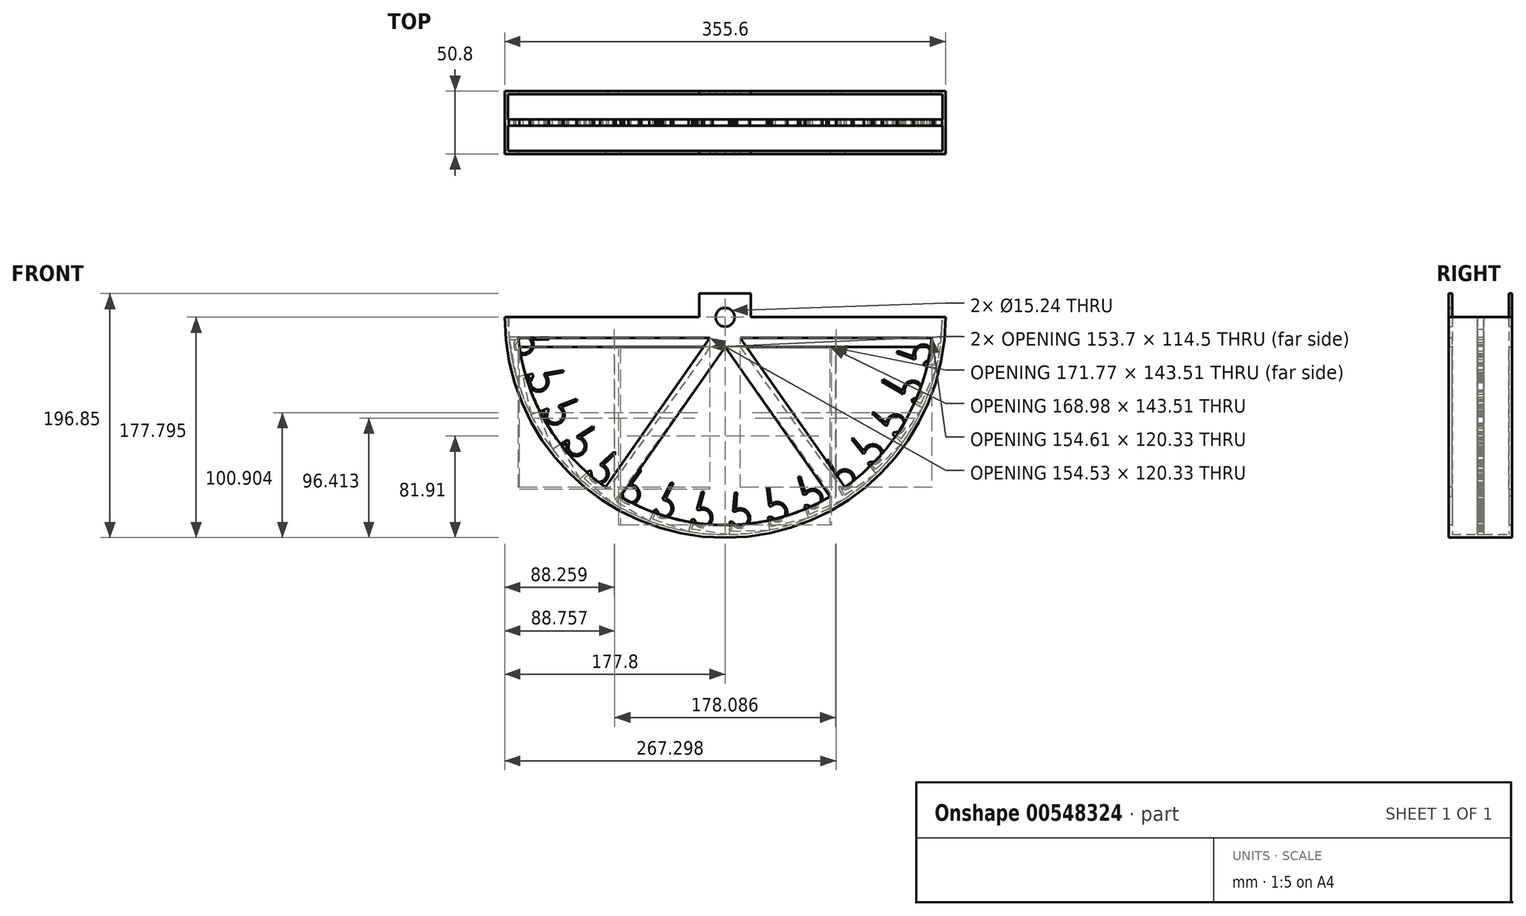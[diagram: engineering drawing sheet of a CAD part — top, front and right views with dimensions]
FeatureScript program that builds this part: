
annotation { "Feature Type Name" : "Feature", "Feature Type Description" : "" }
export const myFeature = defineFeature(function(context is Context, id is Id, definition is map)
    precondition{}
    {
        {
            var Q0;
            Q0=qCreatedBy(makeId("Front.planeOp"),FACE);
            var sketch = newSketch(context, id + "F0", { "sketchPlane" : qUnion([Q0])});
            skArc(sketch, "E0", {"start": v(-177.8, 177.3) * mm, "mid": v(0, -0.5) * mm, "end": v(177.8, 177.3) * mm});
            skLineSegment(sketch, "E1", {"start": v(0, 177.3) * mm, "end": v(177.8, 177.3) * mm});
            skLineSegment(sketch, "E2", {"start": v(0, 177.3) * mm, "end": v(-177.8, 177.3) * mm});
            skLineSegment(sketch, "E3.MirrorCS", {"start": v(-142.3, 159.18) * mm, "end": v(-142.3, 161.09) * mm});
            skLineSegment(sketch, "E4.MirrorCS", {"start": v(-166, 159.36) * mm, "end": v(-166.07, 161.26) * mm});
            skArc(sketch, "E5.MirrorCS", {"start": v(-169.1, 155.45) * mm, "mid": v(-160.47, 148.66) * mm, "end": v(-157.47, 159.21) * mm});
            skLineSegment(sketch, "E6.MirrorCS", {"start": v(-170.16, 157.27) * mm, "end": v(-168.5, 159.37) * mm});
            skLineSegment(sketch, "E7.MirrorCS", {"start": v(-174.1, 159.4) * mm, "end": v(-168.5, 159.37) * mm});
            skLineSegment(sketch, "E8.MirrorCS", {"start": v(-155.76, 159.25) * mm, "end": v(-142.3, 159.18) * mm});
            skLineSegment(sketch, "E9.MirrorCS", {"start": v(-142.3, 161.09) * mm, "end": v(-157.54, 161.16) * mm});
            skArc(sketch, "E10.MirrorCS", {"start": v(-170.16, 157.27) * mm, "mid": v(-161.42, 147.02) * mm, "end": v(-155.76, 159.25) * mm});
            skLineSegment(sketch, "E11.MirrorCS", {"start": v(-166.07, 161.26) * mm, "end": v(-174.53, 161.3) * mm});
            skLineSegment(sketch, "E12.MirrorCS", {"start": v(-166, 159.36) * mm, "end": v(-169.1, 155.45) * mm});
            skLineSegment(sketch, "E13", {"start": v(-174.1, 159.4) * mm, "end": v(-168.5, 129.1) * mm});
            skLineSegment(sketch, "E14", {"start": v(-162.95, 128.2) * mm, "end": v(-156.6, 98.59) * mm});
            skLineSegment(sketch, "E15.MirrorCS", {"start": v(-130.5, 132.86) * mm, "end": v(-130.84, 134.73) * mm});
            skLineSegment(sketch, "E16.MirrorCS", {"start": v(-154.75, 129.7) * mm, "end": v(-155.1, 131.58) * mm});
            skArc(sketch, "E17.MirrorCS", {"start": v(-157.1, 125.2) * mm, "mid": v(-148.27, 119.02) * mm, "end": v(-145.36, 129.4) * mm});
            skLineSegment(sketch, "E18.MirrorCS", {"start": v(-157.54, 129.03) * mm, "end": v(-157.45, 129.2) * mm});
            skLineSegment(sketch, "E19.MirrorCS", {"start": v(-162.95, 128.2) * mm, "end": v(-157.45, 129.2) * mm});
            skLineSegment(sketch, "E20.MirrorCS", {"start": v(-144.3, 130.3) * mm, "end": v(-130.5, 132.86) * mm});
            skLineSegment(sketch, "E21.MirrorCS", {"start": v(-130.84, 134.73) * mm, "end": v(-145.83, 131.96) * mm});
            skArc(sketch, "E22.MirrorCS", {"start": v(-157.54, 129.03) * mm, "mid": v(-149.72, 117.28) * mm, "end": v(-144.3, 130.3) * mm});
            skLineSegment(sketch, "E23.MirrorCS", {"start": v(-145.83, 131.96) * mm, "end": v(-145.36, 129.4) * mm});
            skLineSegment(sketch, "E24.MirrorCS", {"start": v(-155.1, 131.58) * mm, "end": v(-168.5, 129.1) * mm});
            skLineSegment(sketch, "E25.MirrorCS", {"start": v(-154.75, 129.7) * mm, "end": v(-157.1, 125.2) * mm});
            skLineSegment(sketch, "E26.MirrorCS", {"start": v(-119.21, 109.69) * mm, "end": v(-119.9, 111.46) * mm});
            skLineSegment(sketch, "E27.MirrorCS", {"start": v(-142.33, 102.07) * mm, "end": v(-143.02, 103.85) * mm});
            skArc(sketch, "E28.MirrorCS", {"start": v(-143.8, 97.2) * mm, "mid": v(-133.82, 93.07) * mm, "end": v(-133.3, 103.86) * mm});
            skLineSegment(sketch, "E29.MirrorCS", {"start": v(-145.22, 100.13) * mm, "end": v(-144.94, 101.06) * mm});
            skLineSegment(sketch, "E30.MirrorCS", {"start": v(-150.15, 99.04) * mm, "end": v(-144.94, 101.06) * mm});
            skLineSegment(sketch, "E31.MirrorCS", {"start": v(-132.1, 104.69) * mm, "end": v(-119.21, 109.69) * mm});
            skLineSegment(sketch, "E32.MirrorCS", {"start": v(-119.9, 111.46) * mm, "end": v(-134.1, 105.95) * mm});
            skArc(sketch, "E33.MirrorCS", {"start": v(-145.22, 100.13) * mm, "mid": v(-134.73, 91.1) * mm, "end": v(-132.1, 104.69) * mm});
            skLineSegment(sketch, "E34.MirrorCS", {"start": v(-134.1, 105.95) * mm, "end": v(-133.3, 103.86) * mm});
            skLineSegment(sketch, "E35.MirrorCS", {"start": v(-143.02, 103.85) * mm, "end": v(-156.6, 98.59) * mm});
            skLineSegment(sketch, "E36.MirrorCS", {"start": v(-142.33, 102.07) * mm, "end": v(-143.8, 97.2) * mm});
            skLineSegment(sketch, "E37", {"start": v(-174.53, 177.3) * mm, "end": v(-174.53, 161.3) * mm});
            skLineSegment(sketch, "E38", {"start": v(-150.15, 99.04) * mm, "end": v(-139.2, 70.82) * mm});
            skLineSegment(sketch, "E39", {"start": v(-174.53, 161.3) * mm, "end": v(0, 177.3) * mm, "construction": true});
            skLineSegment(sketch, "E40", {"start": v(-168.5, 129.1) * mm, "end": v(0, 177.3) * mm, "construction": true});
            skLineSegment(sketch, "E41", {"start": v(-156.6, 98.59) * mm, "end": v(0, 177.3) * mm, "construction": true});
            skLineSegment(sketch, "E42", {"start": v(-139.2, 70.82) * mm, "end": v(0, 177.3) * mm, "construction": true});
            skLineSegment(sketch, "E43", {"start": v(-174.1, 159.4) * mm, "end": v(-174.45, 161.3) * mm, "construction": true});
            skLineSegment(sketch, "E44", {"start": v(-162.95, 128.2) * mm, "end": v(-163.35, 130.05) * mm, "construction": true});
            skLineSegment(sketch, "E45", {"start": v(-150.15, 99.04) * mm, "end": v(-150.84, 100.82) * mm, "construction": true});
            skLineSegment(sketch, "E46", {"start": v(0, 177.3) * mm, "end": v(-116.96, 46.77) * mm, "construction": true});
            skLineSegment(sketch, "E47", {"start": v(-132.44, 72.79) * mm, "end": v(-116.96, 46.77) * mm});
            skLineSegment(sketch, "E48.MirrorCS", {"start": v(-88.28, 67.45) * mm, "end": v(-89.57, 68.85) * mm});
            skLineSegment(sketch, "E49.MirrorCS", {"start": v(-107.92, 52.51) * mm, "end": v(-109.2, 53.91) * mm});
            skArc(sketch, "E50.MirrorCS", {"start": v(-107.5, 47.45) * mm, "mid": v(-97.11, 46.67) * mm, "end": v(-98.9, 56.94) * mm});
            skLineSegment(sketch, "E51.MirrorCS", {"start": v(-109.3, 47.8) * mm, "end": v(-109.55, 51) * mm});
            skLineSegment(sketch, "E52.MirrorCS", {"start": v(-113.66, 47.22) * mm, "end": v(-109.55, 51) * mm});
            skLineSegment(sketch, "E53.MirrorCS", {"start": v(-98.31, 58.2) * mm, "end": v(-88.28, 67.45) * mm});
            skLineSegment(sketch, "E54.MirrorCS", {"start": v(-89.57, 68.85) * mm, "end": v(-100.78, 58.52) * mm});
            skLineSegment(sketch, "E55.MirrorCS", {"start": v(-109.2, 53.91) * mm, "end": v(-116.96, 46.77) * mm});
            skLineSegment(sketch, "E56.MirrorCS", {"start": v(-107.92, 52.51) * mm, "end": v(-107.5, 47.45) * mm});
            skLineSegment(sketch, "E57", {"start": v(-109.55, 51) * mm, "end": v(-98.31, 58.2) * mm, "construction": true});
            skLineSegment(sketch, "E58", {"start": v(-113.66, 47.22) * mm, "end": v(-90.63, 27.29) * mm});
            skLineSegment(sketch, "E59", {"start": v(-90.63, 27.29) * mm, "end": v(0, 177.3) * mm, "construction": true});
            skLineSegment(sketch, "E60.MirrorCS", {"start": v(-67.5, 53.57) * mm, "end": v(-69.03, 54.7) * mm});
            skLineSegment(sketch, "E61.MirrorCS", {"start": v(-82.81, 34.6) * mm, "end": v(-84.34, 35.75) * mm});
            skArc(sketch, "E62.MirrorCS", {"start": v(-81.47, 29.71) * mm, "mid": v(-70.86, 31.55) * mm, "end": v(-76.08, 40.96) * mm});
            skLineSegment(sketch, "E63.MirrorCS", {"start": v(-87.47, 28.34) * mm, "end": v(-84.14, 32.82) * mm});
            skLineSegment(sketch, "E64.MirrorCS", {"start": v(-75.85, 42.34) * mm, "end": v(-67.5, 53.57) * mm});
            skLineSegment(sketch, "E65.MirrorCS", {"start": v(-69.03, 54.7) * mm, "end": v(-78.12, 42.48) * mm});
            skArc(sketch, "E66.MirrorCS", {"start": v(-83.27, 29.68) * mm, "mid": v(-69.91, 30.35) * mm, "end": v(-75.85, 42.34) * mm});
            skLineSegment(sketch, "E67.MirrorCS", {"start": v(-78.12, 42.48) * mm, "end": v(-76.08, 40.96) * mm});
            skLineSegment(sketch, "E68.MirrorCS", {"start": v(-84.34, 35.75) * mm, "end": v(-90.63, 27.29) * mm});
            skLineSegment(sketch, "E69.MirrorCS", {"start": v(-82.81, 34.6) * mm, "end": v(-81.47, 29.71) * mm});
            skArc(sketch, "E70.trimOffspring", {"start": v(-109.3, 47.8) * mm, "mid": v(-96.5, 45.3) * mm, "end": v(-98.31, 58.2) * mm});
            skLineSegment(sketch, "E71", {"start": v(-82.81, 34.6) * mm, "end": v(-76.08, 40.96) * mm, "construction": true});
            skLineSegment(sketch, "E72", {"start": v(-84.14, 32.82) * mm, "end": v(-83.27, 29.68) * mm});
            skLineSegment(sketch, "E73.MirrorCS", {"start": v(-41.93, 43.33) * mm, "end": v(-43.64, 44.16) * mm});
            skLineSegment(sketch, "E74.MirrorCS", {"start": v(-54.81, 21.7) * mm, "end": v(-56.52, 22.52) * mm});
            skArc(sketch, "E75.MirrorCS", {"start": v(-52.58, 17.13) * mm, "mid": v(-43.55, 21.13) * mm, "end": v(-48.59, 29.62) * mm});
            skLineSegment(sketch, "E76.MirrorCS", {"start": v(-54.18, 16.42) * mm, "end": v(-55.78, 19.7) * mm});
            skLineSegment(sketch, "E77.MirrorCS", {"start": v(-58.23, 14.66) * mm, "end": v(-55.78, 19.7) * mm});
            skLineSegment(sketch, "E78.MirrorCS", {"start": v(-47.96, 30.92) * mm, "end": v(-41.93, 43.33) * mm});
            skLineSegment(sketch, "E79.MirrorCS", {"start": v(-43.64, 44.16) * mm, "end": v(-50.3, 30.46) * mm});
            skArc(sketch, "E80.MirrorCS", {"start": v(-54.18, 16.42) * mm, "mid": v(-42.49, 19.98) * mm, "end": v(-47.96, 30.92) * mm});
            skLineSegment(sketch, "E81.MirrorCS", {"start": v(-50.3, 30.46) * mm, "end": v(-48.59, 29.62) * mm});
            skLineSegment(sketch, "E82.MirrorCS", {"start": v(-56.52, 22.52) * mm, "end": v(-61.13, 13.04) * mm});
            skLineSegment(sketch, "E83.MirrorCS", {"start": v(-54.81, 21.7) * mm, "end": v(-52.58, 17.13) * mm});
            skLineSegment(sketch, "E84", {"start": v(0, 177.3) * mm, "end": v(-29.92, 2.03) * mm, "construction": true});
            skLineSegment(sketch, "E85", {"start": v(-58.23, 14.66) * mm, "end": v(-29.5, 4.54) * mm});
            skLineSegment(sketch, "E86", {"start": v(-55.78, 19.7) * mm, "end": v(-48.59, 29.62) * mm, "construction": true});
            skLineSegment(sketch, "E87", {"start": v(0, 177.3) * mm, "end": v(3.21, -0.48) * mm, "construction": true});
            skLineSegment(sketch, "E88", {"start": v(0, 177.3) * mm, "end": v(36.24, 3.23) * mm, "construction": true});
            skLineSegment(sketch, "E89", {"start": v(0, 177.3) * mm, "end": v(68, 13.01) * mm, "construction": true});
            skLineSegment(sketch, "E90", {"start": v(0, 177.3) * mm, "end": v(97.38, 28.54) * mm, "construction": true});
            skLineSegment(sketch, "E91", {"start": v(0, 177.3) * mm, "end": v(123.37, 49.26) * mm, "construction": true});
            skLineSegment(sketch, "E92", {"start": v(0, 177.3) * mm, "end": v(145.04, 74.45) * mm, "construction": true});
            skLineSegment(sketch, "E93.MirrorCS", {"start": v(-16.96, 36.4) * mm, "end": v(-18.8, 36.9) * mm});
            skLineSegment(sketch, "E94.MirrorCS", {"start": v(-24.9, 14.2) * mm, "end": v(-26.74, 14.7) * mm});
            skArc(sketch, "E95.MirrorCS", {"start": v(-21.85, 10.14) * mm, "mid": v(-11.66, 15.16) * mm, "end": v(-20.95, 21.7) * mm});
            skLineSegment(sketch, "E96.MirrorCS", {"start": v(-24.1, 10.23) * mm, "end": v(-25.48, 12.06) * mm});
            skLineSegment(sketch, "E97.MirrorCS", {"start": v(-26.94, 6.67) * mm, "end": v(-25.48, 12.06) * mm});
            skLineSegment(sketch, "E98.MirrorCS", {"start": v(-20.5, 23.35) * mm, "end": v(-16.96, 36.4) * mm});
            skLineSegment(sketch, "E99.MirrorCS", {"start": v(-18.8, 36.9) * mm, "end": v(-22.79, 22.2) * mm});
            skArc(sketch, "E100.MirrorCS", {"start": v(-24.1, 10.23) * mm, "mid": v(-10.53, 13.55) * mm, "end": v(-20.5, 23.35) * mm});
            skLineSegment(sketch, "E101.MirrorCS", {"start": v(-22.79, 22.2) * mm, "end": v(-20.95, 21.7) * mm});
            skLineSegment(sketch, "E102.MirrorCS", {"start": v(-26.74, 14.7) * mm, "end": v(-29.5, 4.54) * mm});
            skLineSegment(sketch, "E103.MirrorCS", {"start": v(-24.9, 14.2) * mm, "end": v(-21.85, 10.14) * mm});
            skLineSegment(sketch, "E104", {"start": v(-26.94, 6.67) * mm, "end": v(3.17, 2.06) * mm});
            skLineSegment(sketch, "E105", {"start": v(-25.48, 12.06) * mm, "end": v(-20.95, 21.7) * mm, "construction": true});
            skLineSegment(sketch, "E106", {"start": v(0, 177.3) * mm, "end": v(-61.13, 13.04) * mm, "construction": true});
            skLineSegment(sketch, "E107.MirrorCS", {"start": v(9.56, 35.7) * mm, "end": v(7.66, 35.86) * mm});
            skLineSegment(sketch, "E108.MirrorCS", {"start": v(5.89, 12.42) * mm, "end": v(3.99, 12.57) * mm});
            skArc(sketch, "E109.MirrorCS", {"start": v(9.64, 9) * mm, "mid": v(18.72, 15.82) * mm, "end": v(8.37, 20.51) * mm});
            skLineSegment(sketch, "E110.MirrorCS", {"start": v(7.4, 8.66) * mm, "end": v(5.71, 10.2) * mm});
            skLineSegment(sketch, "E111.MirrorCS", {"start": v(5.28, 4.64) * mm, "end": v(5.71, 10.2) * mm});
            skLineSegment(sketch, "E112.MirrorCS", {"start": v(8.5, 22.22) * mm, "end": v(9.56, 35.7) * mm});
            skLineSegment(sketch, "E113.MirrorCS", {"start": v(7.66, 35.86) * mm, "end": v(6.47, 20.66) * mm});
            skArc(sketch, "E114.MirrorCS", {"start": v(7.4, 8.66) * mm, "mid": v(20.13, 14.45) * mm, "end": v(8.5, 22.22) * mm});
            skLineSegment(sketch, "E115.MirrorCS", {"start": v(6.47, 20.66) * mm, "end": v(8.37, 20.51) * mm});
            skLineSegment(sketch, "E116.MirrorCS", {"start": v(3.99, 12.57) * mm, "end": v(3.17, 2.06) * mm});
            skLineSegment(sketch, "E117.MirrorCS", {"start": v(5.89, 12.42) * mm, "end": v(9.64, 9) * mm});
            skLineSegment(sketch, "E118", {"start": v(5.71, 10.2) * mm, "end": v(8.37, 20.51) * mm, "construction": true});
            skLineSegment(sketch, "E119", {"start": v(5.28, 4.64) * mm, "end": v(35.72, 5.71) * mm});
            skLineSegment(sketch, "E120.MirrorCS", {"start": v(35.74, 39.96) * mm, "end": v(33.85, 39.75) * mm});
            skLineSegment(sketch, "E121.MirrorCS", {"start": v(36.47, 16.4) * mm, "end": v(34.57, 16.2) * mm});
            skArc(sketch, "E122.MirrorCS", {"start": v(40.79, 13.73) * mm, "mid": v(48.44, 22.12) * mm, "end": v(37.4, 24.81) * mm});
            skLineSegment(sketch, "E123.MirrorCS", {"start": v(38.66, 12.99) * mm, "end": v(36.7, 14.19) * mm});
            skLineSegment(sketch, "E124.MirrorCS", {"start": v(37.32, 8.63) * mm, "end": v(36.7, 14.19) * mm});
            skLineSegment(sketch, "E125.MirrorCS", {"start": v(37.22, 26.51) * mm, "end": v(35.74, 39.96) * mm});
            skLineSegment(sketch, "E126.MirrorCS", {"start": v(33.85, 39.75) * mm, "end": v(35.5, 24.6) * mm});
            skArc(sketch, "E127.MirrorCS", {"start": v(38.66, 12.99) * mm, "mid": v(50.08, 21.04) * mm, "end": v(37.22, 26.51) * mm});
            skLineSegment(sketch, "E128.MirrorCS", {"start": v(35.5, 24.6) * mm, "end": v(37.4, 24.81) * mm});
            skLineSegment(sketch, "E129.MirrorCS", {"start": v(34.57, 16.2) * mm, "end": v(35.72, 5.71) * mm});
            skLineSegment(sketch, "E130.MirrorCS", {"start": v(36.47, 16.4) * mm, "end": v(40.79, 13.73) * mm});
            skLineSegment(sketch, "E131", {"start": v(36.7, 14.19) * mm, "end": v(37.4, 24.81) * mm, "construction": true});
            skLineSegment(sketch, "E132", {"start": v(37.32, 8.63) * mm, "end": v(67.03, 15.36) * mm});
            skLineSegment(sketch, "E133.MirrorCS", {"start": v(60.67, 49.01) * mm, "end": v(58.85, 48.45) * mm});
            skLineSegment(sketch, "E134.MirrorCS", {"start": v(65.77, 26) * mm, "end": v(63.95, 25.44) * mm});
            skArc(sketch, "E135.MirrorCS", {"start": v(70.51, 24.18) * mm, "mid": v(76.47, 33.85) * mm, "end": v(65.13, 34.44) * mm});
            skLineSegment(sketch, "E136.MirrorCS", {"start": v(68.56, 23.05) * mm, "end": v(66.42, 23.87) * mm});
            skLineSegment(sketch, "E137.MirrorCS", {"start": v(68.05, 18.53) * mm, "end": v(66.42, 23.87) * mm});
            skLineSegment(sketch, "E138.MirrorCS", {"start": v(64.63, 36.07) * mm, "end": v(60.67, 49.01) * mm});
            skLineSegment(sketch, "E139.MirrorCS", {"start": v(58.85, 48.45) * mm, "end": v(63.3, 33.88) * mm});
            skArc(sketch, "E140.MirrorCS", {"start": v(68.56, 23.05) * mm, "mid": v(78.29, 33.1) * mm, "end": v(64.63, 36.07) * mm});
            skLineSegment(sketch, "E141.MirrorCS", {"start": v(63.3, 33.88) * mm, "end": v(65.13, 34.44) * mm});
            skLineSegment(sketch, "E142.MirrorCS", {"start": v(63.95, 25.44) * mm, "end": v(67.03, 15.36) * mm});
            skLineSegment(sketch, "E143.MirrorCS", {"start": v(65.77, 26) * mm, "end": v(70.51, 24.18) * mm});
            skLineSegment(sketch, "E144", {"start": v(66.42, 23.87) * mm, "end": v(65.13, 34.44) * mm, "construction": true});
            skLineSegment(sketch, "E145", {"start": v(68.05, 18.53) * mm, "end": v(96, 30.66) * mm});
            skLineSegment(sketch, "E146.MirrorCS", {"start": v(83.49, 62.54) * mm, "end": v(81.8, 61.66) * mm});
            skLineSegment(sketch, "E147.MirrorCS", {"start": v(92.78, 40.88) * mm, "end": v(91.1, 40) * mm});
            skArc(sketch, "E148.MirrorCS", {"start": v(97.78, 39.97) * mm, "mid": v(101.83, 50.59) * mm, "end": v(90.57, 49.05) * mm});
            skLineSegment(sketch, "E149.MirrorCS", {"start": v(96.06, 38.5) * mm, "end": v(93.81, 38.91) * mm});
            skLineSegment(sketch, "E150.MirrorCS", {"start": v(96.41, 33.96) * mm, "end": v(93.81, 38.91) * mm});
            skLineSegment(sketch, "E151.MirrorCS", {"start": v(89.78, 50.57) * mm, "end": v(83.49, 62.54) * mm});
            skLineSegment(sketch, "E152.MirrorCS", {"start": v(81.8, 61.66) * mm, "end": v(88.89, 48.17) * mm});
            skArc(sketch, "E153.MirrorCS", {"start": v(96.06, 38.5) * mm, "mid": v(103.75, 50.18) * mm, "end": v(89.78, 50.57) * mm});
            skLineSegment(sketch, "E154.MirrorCS", {"start": v(88.89, 48.17) * mm, "end": v(90.57, 49.05) * mm});
            skLineSegment(sketch, "E155.MirrorCS", {"start": v(91.1, 40) * mm, "end": v(96, 30.66) * mm});
            skLineSegment(sketch, "E156.MirrorCS", {"start": v(92.78, 40.88) * mm, "end": v(97.78, 39.97) * mm});
            skLineSegment(sketch, "E157", {"start": v(93.81, 38.91) * mm, "end": v(90.57, 49.05) * mm, "construction": true});
            skLineSegment(sketch, "E158", {"start": v(96.41, 33.96) * mm, "end": v(121.6, 51.09) * mm});
            skLineSegment(sketch, "E159.MirrorCS", {"start": v(103.38, 80.08) * mm, "end": v(101.9, 78.9) * mm});
            skLineSegment(sketch, "E160.MirrorCS", {"start": v(116.54, 60.53) * mm, "end": v(115.05, 59.34) * mm});
            skArc(sketch, "E161.MirrorCS", {"start": v(121.62, 60.57) * mm, "mid": v(123.63, 71.75) * mm, "end": v(112.86, 68.15) * mm});
            skLineSegment(sketch, "E162.MirrorCS", {"start": v(120.21, 58.8) * mm, "end": v(117.93, 58.79) * mm});
            skLineSegment(sketch, "E163.MirrorCS", {"start": v(121.4, 54.4) * mm, "end": v(117.93, 58.79) * mm});
            skLineSegment(sketch, "E164.MirrorCS", {"start": v(111.8, 69.49) * mm, "end": v(103.38, 80.08) * mm});
            skLineSegment(sketch, "E165.MirrorCS", {"start": v(101.9, 78.9) * mm, "end": v(111.37, 66.96) * mm});
            skArc(sketch, "E166.MirrorCS", {"start": v(120.21, 58.8) * mm, "mid": v(125.6, 71.7) * mm, "end": v(111.8, 69.49) * mm});
            skLineSegment(sketch, "E167.MirrorCS", {"start": v(111.37, 66.96) * mm, "end": v(112.86, 68.15) * mm});
            skLineSegment(sketch, "E168.MirrorCS", {"start": v(115.05, 59.34) * mm, "end": v(121.6, 51.09) * mm});
            skLineSegment(sketch, "E169.MirrorCS", {"start": v(116.54, 60.53) * mm, "end": v(121.62, 60.57) * mm});
            skLineSegment(sketch, "E170", {"start": v(117.93, 58.79) * mm, "end": v(112.86, 68.15) * mm, "construction": true});
            skLineSegment(sketch, "E171", {"start": v(121.4, 54.4) * mm, "end": v(142.97, 75.92) * mm});
            skLineSegment(sketch, "E172", {"start": v(142.97, 75.92) * mm, "end": v(96.82, 115.8) * mm});
            skLineSegment(sketch, "E173.MirrorCS", {"start": v(119.67, 101.02) * mm, "end": v(118.42, 99.58) * mm});
            skLineSegment(sketch, "E174.MirrorCS", {"start": v(136.24, 84.26) * mm, "end": v(135, 82.82) * mm});
            skArc(sketch, "E175.MirrorCS", {"start": v(141.22, 85.24) * mm, "mid": v(141.11, 96.6) * mm, "end": v(131.2, 91.06) * mm});
            skLineSegment(sketch, "E176.MirrorCS", {"start": v(140.17, 83.25) * mm, "end": v(137.92, 82.8) * mm});
            skLineSegment(sketch, "E177.MirrorCS", {"start": v(142.15, 79.15) * mm, "end": v(137.92, 82.8) * mm});
            skLineSegment(sketch, "E178.MirrorCS", {"start": v(129.9, 92.17) * mm, "end": v(119.67, 101.02) * mm});
            skLineSegment(sketch, "E179.MirrorCS", {"start": v(118.42, 99.58) * mm, "end": v(129.95, 89.61) * mm});
            skArc(sketch, "E180.MirrorCS", {"start": v(140.17, 83.25) * mm, "mid": v(143.05, 96.92) * mm, "end": v(129.9, 92.17) * mm});
            skLineSegment(sketch, "E181.MirrorCS", {"start": v(129.95, 89.61) * mm, "end": v(131.2, 91.06) * mm});
            skLineSegment(sketch, "E182.MirrorCS", {"start": v(135, 82.82) * mm, "end": v(142.97, 75.92) * mm});
            skLineSegment(sketch, "E183.MirrorCS", {"start": v(136.24, 84.26) * mm, "end": v(141.22, 85.24) * mm});
            skLineSegment(sketch, "E184", {"start": v(137.92, 82.8) * mm, "end": v(131.2, 91.06) * mm, "construction": true});
            skLineSegment(sketch, "E185", {"start": v(0, 177.3) * mm, "end": v(161.64, 103.24) * mm, "construction": true});
            skLineSegment(sketch, "E186", {"start": v(0, 177.3) * mm, "end": v(172.6, 134.62) * mm, "construction": true});
            skLineSegment(sketch, "E187", {"start": v(142.15, 79.15) * mm, "end": v(159.33, 104.3) * mm});
            skLineSegment(sketch, "E188.MirrorCS", {"start": v(127.38, 127.17) * mm, "end": v(126.42, 125.52) * mm});
            skLineSegment(sketch, "E189.MirrorCS", {"start": v(151.17, 111.23) * mm, "end": v(150.22, 109.59) * mm});
            skArc(sketch, "E190.MirrorCS", {"start": v(155.89, 113.13) * mm, "mid": v(153.67, 124.27) * mm, "end": v(144.96, 116.98) * mm});
            skLineSegment(sketch, "E191.MirrorCS", {"start": v(155.22, 110.97) * mm, "end": v(153.1, 110.12) * mm});
            skLineSegment(sketch, "E192.MirrorCS", {"start": v(157.93, 107.32) * mm, "end": v(153.1, 110.12) * mm});
            skLineSegment(sketch, "E193.MirrorCS", {"start": v(143.47, 117.84) * mm, "end": v(127.38, 127.17) * mm});
            skLineSegment(sketch, "E194.MirrorCS", {"start": v(126.42, 125.52) * mm, "end": v(144, 115.33) * mm});
            skArc(sketch, "E195.MirrorCS", {"start": v(155.22, 110.97) * mm, "mid": v(155.51, 124.95) * mm, "end": v(143.47, 117.84) * mm});
            skLineSegment(sketch, "E196.MirrorCS", {"start": v(144, 115.33) * mm, "end": v(144.96, 116.98) * mm});
            skLineSegment(sketch, "E197.MirrorCS", {"start": v(150.22, 109.59) * mm, "end": v(159.33, 104.3) * mm});
            skLineSegment(sketch, "E198.MirrorCS", {"start": v(151.17, 111.23) * mm, "end": v(155.89, 113.13) * mm});
            skLineSegment(sketch, "E199", {"start": v(153.1, 110.12) * mm, "end": v(144.96, 116.98) * mm, "construction": true});
            skLineSegment(sketch, "E200", {"start": v(157.93, 107.32) * mm, "end": v(170.14, 135.22) * mm});
            skLineSegment(sketch, "E201.MirrorCS", {"start": v(139.27, 150.07) * mm, "end": v(138.64, 148.27) * mm});
            skLineSegment(sketch, "E202.MirrorCS", {"start": v(160.82, 140.52) * mm, "end": v(160.2, 138.72) * mm});
            skArc(sketch, "E203.MirrorCS", {"start": v(165.1, 143.26) * mm, "mid": v(160.85, 153.8) * mm, "end": v(153.65, 145) * mm});
            skLineSegment(sketch, "E204.MirrorCS", {"start": v(164.85, 141.02) * mm, "end": v(162.92, 139.78) * mm});
            skLineSegment(sketch, "E205.MirrorCS", {"start": v(168.2, 137.93) * mm, "end": v(162.92, 139.78) * mm});
            skLineSegment(sketch, "E206.MirrorCS", {"start": v(152.03, 145.57) * mm, "end": v(139.27, 150.07) * mm});
            skLineSegment(sketch, "E207.MirrorCS", {"start": v(138.64, 148.27) * mm, "end": v(153.02, 143.2) * mm});
            skArc(sketch, "E208.MirrorCS", {"start": v(164.85, 141.02) * mm, "mid": v(162.54, 154.8) * mm, "end": v(152.03, 145.57) * mm});
            skLineSegment(sketch, "E209.MirrorCS", {"start": v(153.02, 143.2) * mm, "end": v(153.65, 145) * mm});
            skLineSegment(sketch, "E210.MirrorCS", {"start": v(160.2, 138.72) * mm, "end": v(170.14, 135.22) * mm});
            skLineSegment(sketch, "E211.MirrorCS", {"start": v(160.82, 140.52) * mm, "end": v(165.1, 143.26) * mm});
            skLineSegment(sketch, "E212", {"start": v(162.92, 139.78) * mm, "end": v(153.65, 145) * mm, "construction": true});
            skLineSegment(sketch, "E213", {"start": v(0, 177.3) * mm, "end": v(177.53, 167.48) * mm, "construction": true});
            skLineSegment(sketch, "E214", {"start": v(168.2, 137.93) * mm, "end": v(175, 167.62) * mm});
            skLineSegment(sketch, "E215", {"start": v(175, 167.62) * mm, "end": v(175, 177.3) * mm});
            skLineSegment(sketch, "E216", {"start": v(-87.47, 28.34) * mm, "end": v(-61.13, 13.04) * mm});
            skLineSegment(sketch, "E217", {"start": v(-20.86, 177.3) * mm, "end": v(-20.86, 196.35) * mm});
            skCircle(sketch, "E218", {"center": v(0, 177.3) * mm, "radius": 7.62 * mm});
            skLineSegment(sketch, "E219.MirrorCS", {"start": v(-105.56, 87.5) * mm, "end": v(-106.56, 89.12) * mm});
            skLineSegment(sketch, "E220.MirrorCS", {"start": v(-125.85, 76.9) * mm, "end": v(-126.85, 78.51) * mm});
            skArc(sketch, "E221.MirrorCS", {"start": v(-126.39, 71.85) * mm, "mid": v(-115.2, 68.69) * mm, "end": v(-118.7, 79.77) * mm});
            skLineSegment(sketch, "E222.MirrorCS", {"start": v(-127.8, 74.76) * mm, "end": v(-127.7, 75.74) * mm});
            skLineSegment(sketch, "E223.MirrorCS", {"start": v(-132.44, 72.79) * mm, "end": v(-127.7, 75.74) * mm});
            skLineSegment(sketch, "E224.MirrorCS", {"start": v(-116.66, 80.58) * mm, "end": v(-105.56, 87.5) * mm});
            skLineSegment(sketch, "E225.MirrorCS", {"start": v(-106.56, 89.12) * mm, "end": v(-119.5, 81.06) * mm});
            skArc(sketch, "E226.MirrorCS", {"start": v(-127.8, 74.76) * mm, "mid": v(-116.24, 66.2) * mm, "end": v(-116.66, 80.58) * mm});
            skLineSegment(sketch, "E227.MirrorCS", {"start": v(-119.5, 81.06) * mm, "end": v(-118.7, 79.77) * mm});
            skLineSegment(sketch, "E228.MirrorCS", {"start": v(-126.85, 78.51) * mm, "end": v(-139.2, 70.82) * mm});
            skLineSegment(sketch, "E229.MirrorCS", {"start": v(-125.85, 76.9) * mm, "end": v(-126.39, 71.85) * mm});
            skLineSegment(sketch, "E230", {"start": v(-98.9, 56.94) * mm, "end": v(-100.78, 58.52) * mm});
            skLineSegment(sketch, "E231", {"start": v(-20.86, 196.35) * mm, "end": v(0, 196.35) * mm});
            skLineSegment(sketch, "E232.MirrorCS", {"start": v(20.86, 196.35) * mm, "end": v(0, 196.35) * mm});
            skLineSegment(sketch, "E233.MirrorCS", {"start": v(20.86, 177.3) * mm, "end": v(20.86, 196.35) * mm});
            skLineSegment(sketch, "E234", {"start": v(-157.47, 159.21) * mm, "end": v(-157.54, 161.16) * mm});
            skSolve(sketch);
        }
        {
            var Q0;
            Q0 = qSketchRegion(id + "F0", true);
            extrude(context, id + "F1", {"entities" : qUnion([Q0]), "endBound" : BoundingType.SYMMETRIC, "depth" : 50.8 * mm, "offsetDistance" : 25.4 * mm});
        }
        {
            var Q0;
            Q0=makeQuery(id+"F1.opExtrude","SWEPT_FACE",FACE,{"disambiguationData":[OSD([sQuery(id+"F0.wireOp",EDGE,"E1"),sQuery(id+"F0.wireOp",EDGE,"E2")])]});
            var Q1;
            Q1=makeQuery(id+"F1.opExtrude","SWEPT_FACE",FACE,{"disambiguationData":[OSD([sQuery(id+"F0.wireOp",EDGE,"E217")])]});
            var Q2;
            Q2=makeQuery(id+"F1.opExtrude","SWEPT_FACE",FACE,{"disambiguationData":[OSD([sQuery(id+"F0.wireOp",EDGE,"IKzNIRuS-lt9D-PZX5-G1JW-kbrlMgvdaDML")])]});
            var Q3;
            Q3=makeQuery(id+"F1.opExtrude","SWEPT_FACE",FACE,{"disambiguationData":[OSD([sQuery(id+"F0.wireOp",EDGE,"ju7AKv3p-tV9e-Mq4A-qTnI-Takg7eoSyEy9")])]});
            shell(context, id + "F2", {"entities" : qUnion([Q0, Q1, Q2, Q3]), "thickness" : 2.54 * mm});
        }
        {
            var Q0;
            {var subQ0=sQuery(id+"F0.wireOp",EDGE,"8sBSUSAj-00hb-c3g1-GJDK-NZvKGYPpUrdB");Q0=makeQuery(id+"F0.imprint","IMPRINT",FACE,{"disambiguationData":[TD([[makeQuery(id+"F0.imprint","IMPRINT",EDGE,{"derivedFrom":subQ0}),-1.0]])]});}
            var Q1;
            Q1=makeQuery(id+"F0.imprint","IMPRINT",FACE,{"disambiguationData":[TD([[makeQuery(id+"F0.imprint","IMPRINT",EDGE,{"derivedFrom":sQuery(id+"F0.wireOp",EDGE,"E3.MirrorCS")}),1.0]])]});
            extrude(context, id + "F3", {"entities" : qUnion([Q0, Q1]), "operationType" : NewBodyOperationType.ADD, "endBound" : BoundingType.SYMMETRIC, "depth" : 5.08 * mm, "offsetDistance" : 25.4 * mm});
        }
        {
            var Q0;
            Q0=makeQuery(id+"F1.opExtrude","CAP_FACE",FACE,{"disambiguationData":[OSD([sQuery(id+"F0.wireOp",EDGE,"E0"),sQuery(id+"F0.wireOp",EDGE,"E1"),sQuery(id+"F0.wireOp",EDGE,"E2"),sQuery(id+"F0.wireOp",EDGE,"4NdIO9du-pqLB-0gZj-tUX9-g2KgcOWVYO3W")])],"isStart":false});
            var sketch = newSketch(context, id + "F4", { "sketchPlane" : qUnion([Q0])});
            skArc(sketch, "E235.0", {"start": v(-166.8, 160.57) * mm, "mid": v(-144.76, 92.76) * mm, "end": v(-96.53, 40.24) * mm});
            skLineSegment(sketch, "E236", {"start": v(0, 153.17) * mm, "end": v(-84.49, 32.5) * mm});
            skLineSegment(sketch, "E237", {"start": v(-12.28, 160.57) * mm, "end": v(-96.53, 40.24) * mm});
            skLineSegment(sketch, "E238", {"start": v(-12.28, 160.57) * mm, "end": v(-166.8, 160.57) * mm});
            skLineSegment(sketch, "E239.MirrorCS", {"start": v(12.2, 160.53) * mm, "end": v(166.8, 160.57) * mm});
            skLineSegment(sketch, "E240.MirrorCS", {"start": v(0, 153.17) * mm, "end": v(84.49, 32.5) * mm});
            skLineSegment(sketch, "E241.MirrorCS", {"start": v(12.2, 160.53) * mm, "end": v(96.53, 40.24) * mm});
            skArc(sketch, "E242.trimOffspring", {"start": v(-84.49, 32.5) * mm, "mid": v(0, 9.66) * mm, "end": v(84.49, 32.5) * mm});
            skArc(sketch, "E243.trimOffspring", {"start": v(96.53, 40.24) * mm, "mid": v(144.76, 92.76) * mm, "end": v(166.8, 160.57) * mm});
            skSolve(sketch);
        }
        {
            var Q0;
            Q0 = qSketchRegion(id + "F4", true);
            extrude(context, id + "F5", {"entities" : qUnion([Q0]), "operationType" : NewBodyOperationType.REMOVE, "endBound" : BoundingType.UP_TO_NEXT, "oppositeDirection" : true, "depth" : 25.4 * mm, "offsetDistance" : 25.4 * mm});
        }
        {
            var Q0;
            Q0=makeQuery(id+"F1.opExtrude","CAP_FACE",FACE,{"disambiguationData":[OSD([sQuery(id+"F0.wireOp",EDGE,"E0"),sQuery(id+"F0.wireOp",EDGE,"E1"),sQuery(id+"F0.wireOp",EDGE,"E2"),sQuery(id+"F0.wireOp",EDGE,"E217"),sQuery(id+"F0.wireOp",EDGE,"E218"),sQuery(id+"F0.wireOp",EDGE,"E231"),sQuery(id+"F0.wireOp",EDGE,"E232.MirrorCS"),sQuery(id+"F0.wireOp",EDGE,"E233.MirrorCS")])],"isStart":true});
            var sketch = newSketch(context, id + "F6", { "sketchPlane" : qUnion([Q0])});
            skArc(sketch, "E244.0", {"start": v(165.9, 153.17) * mm, "mid": v(142.12, 88.38) * mm, "end": v(94.25, 38.66) * mm});
            skLineSegment(sketch, "E245", {"start": v(0, 153.17) * mm, "end": v(-85.88, 33.33) * mm});
            skLineSegment(sketch, "E246", {"start": v(-12.2, 153.17) * mm, "end": v(-94.25, 38.66) * mm});
            skLineSegment(sketch, "E247", {"start": v(-12.2, 153.17) * mm, "end": v(-165.9, 153.17) * mm});
            skLineSegment(sketch, "E248.MirrorCS", {"start": v(0, 153.17) * mm, "end": v(85.88, 33.33) * mm});
            skLineSegment(sketch, "E249.MirrorCS", {"start": v(12.2, 153.17) * mm, "end": v(94.25, 38.66) * mm});
            skLineSegment(sketch, "E250.MirrorCS", {"start": v(12.2, 153.17) * mm, "end": v(165.9, 153.17) * mm});
            skArc(sketch, "E251.trimOffspring", {"start": v(-94.25, 38.66) * mm, "mid": v(-142.12, 88.38) * mm, "end": v(-165.9, 153.17) * mm});
            skArc(sketch, "E252.trimOffspring", {"start": v(85.88, 33.33) * mm, "mid": v(0, 9.66) * mm, "end": v(-85.88, 33.33) * mm});
            skSolve(sketch);
        }
        {
            var Q0;
            Q0 = qSketchRegion(id + "F6", true);
            extrude(context, id + "F7", {"entities" : qUnion([Q0]), "operationType" : NewBodyOperationType.REMOVE, "endBound" : BoundingType.UP_TO_NEXT, "oppositeDirection" : true, "depth" : 25.4 * mm, "offsetDistance" : 25.4 * mm});
        }
        {
            var Q0;
            Q0=makeQuery(id+"F1.opExtrude","SWEPT_FACE",FACE,{"disambiguationData":[OSD([sQuery(id+"F0.wireOp",EDGE,"E233.MirrorCS")])]});
            var sketch = newSketch(context, id + "F8", { "sketchPlane" : qUnion([Q0])});
            skLineSegment(sketch, "E253", {"start": v(-22.86, 177.3) * mm, "end": v(-22.86, 196.35) * mm});
            skLineSegment(sketch, "E254", {"start": v(-22.86, 196.35) * mm, "end": v(22.86, 196.35) * mm});
            skLineSegment(sketch, "E255", {"start": v(22.86, 196.35) * mm, "end": v(22.86, 177.3) * mm});
            skLineSegment(sketch, "E256", {"start": v(22.86, 177.3) * mm, "end": v(22.86, 161.97) * mm});
            skLineSegment(sketch, "E257", {"start": v(22.86, 161.97) * mm, "end": v(-22.86, 161.97) * mm});
            skLineSegment(sketch, "E258", {"start": v(-22.86, 161.97) * mm, "end": v(-22.86, 177.3) * mm});
            skSolve(sketch);
        }
        {
            var Q0;
            Q0=makeQuery(id+"F8.imprint","IMPRINT",FACE,{"disambiguationData":[TD([[makeQuery(id+"F8.imprint","IMPRINT",EDGE,{"derivedFrom":sQuery(id+"F8.wireOp",EDGE,"E256")}),-1.0]])]});
            var Q1;
            Q1=makeQuery(id+"F8.imprint","IMPRINT",FACE,{"disambiguationData":[TD([[makeQuery(id+"F8.imprint","IMPRINT",EDGE,{"derivedFrom":sQuery(id+"F8.wireOp",EDGE,"E253")}),-1.0]])]});
            extrude(context, id + "F9", {"entities" : qUnion([Q0, Q1]), "operationType" : NewBodyOperationType.REMOVE, "oppositeDirection" : true, "depth" : 52.07 * mm, "offsetDistance" : 25.4 * mm});
        }
    });
